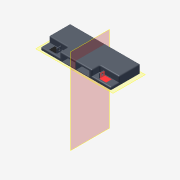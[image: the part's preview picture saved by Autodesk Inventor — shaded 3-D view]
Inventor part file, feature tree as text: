
AUTODESK INVENTOR PART (.ipt)
format: ipt  version: 2014 SP1 (Build 180222100, 222)  size: 363,008 bytes
history: native  units: mm (DEFAULTED — no unit token found)
features: sketch x10, extrude x9, fillet x5, plane x5, mirror x3, split x3, hole x1
ambient origin geometry x8: Origin, YZ Plane, XZ Plane, XY Plane, X Axis, Y Axis, Z Axis, Center Point
bodies: Solid1 (feature_tree)
feature tree (36):
  extrude  "Extrusion1"  Depth=74.422mm
  extrude  "Extrusion2"  Depth=139.7mm TaperAngle=0.0deg
  extrude  "Extrusion3"  Depth=21.336mm
  fillet  "Fillet1"  Radius=14.224mm
  fillet  "Fillet3"  Radius=2.54mm
  fillet  "Fillet4"  Radius=2.54mm
  extrude  "Extrusion4"  Depth=0.254mm TaperAngle=0.0deg
  extrude  "Extrusion5"  Depth=12.7mm TaperAngle=0.0deg
  extrude  "Extrusion6"  Depth=12.7mm TaperAngle=0.0deg
  plane  "Work Plane1"
  mirror  "Mirror1"
  mirror  "Mirror2"
  extrude  "Extrusion7"  Depth=20.32mm
  extrude  "Extrusion8"  Depth=19.558mm TaperAngle=0.0deg
  plane  "Work Plane2"
  fillet  "Fillet5"  Radius=33.02mm
  plane  "Work Plane3"
  extrude  "Extrusion9"  Depth=19.05mm TaperAngle=0.0deg
  hole  "Hole1"  [1 undecoded]
  fillet  "Fillet6"  Radius=56.261mm
  mirror  "Mirror3"
  plane  "Work Plane4"
  split  "Split2"
  plane  "Work Plane6"
  split  "Split3"
  split  "Split4"
  sketch  "Sketch1"  dims[d0=179.578mm d1=74.422mm]
  sketch  "Sketch2"  dims[d2=139.7mm d3=0.0mm d4=21.082mm d5=0.0mm]
  sketch  "Sketch3"  dims[d6=49.276mm d7=21.336mm d8=14.224mm d9=0.0mm d10=2.54mm d12=2.54mm]
  sketch  "Sketch4"  dims[d13=2.54mm d14=0.254mm d15=0.0mm]
  sketch  "Sketch5"  dims[d16=1.524mm d17=12.7mm d18=0.0mm]
  sketch  "Sketch6"  dims[d19=5.08mm d20=12.7mm d21=0.0mm]
  sketch  "Sketch7"  dims[d22=20.32mm d23=20.32mm]
  sketch  "Sketch8"  dims[d24=63.5mm d25=19.558mm d26=0.0mm d27=33.02mm]
  sketch  "Sketch9"  dims[d28=3.048mm d29=19.05mm d30=0.0mm]
  sketch  "Sketch10"  dims[d31=181.102mm d32=-127.0mm d34=1.27mm d35=56.261mm d36=11.9888mm d37=11.5062mm d38=2.0066mm d39=0.0mm d40=5.4864mm d41=5.4864mm d42=19.05mm d43=9.525mm d44=6.35mm d45=14.3117mm d46=25.4mm d47=20.594885mm d48=1.27mm d49=14.986mm d50=90.0deg d51=0.0mm]
note: 1 required parameter value undecoded (feature->parameter linkage not recoverable at this tier; creation-order binding heuristic only, values carry confidence <= 0.55)
